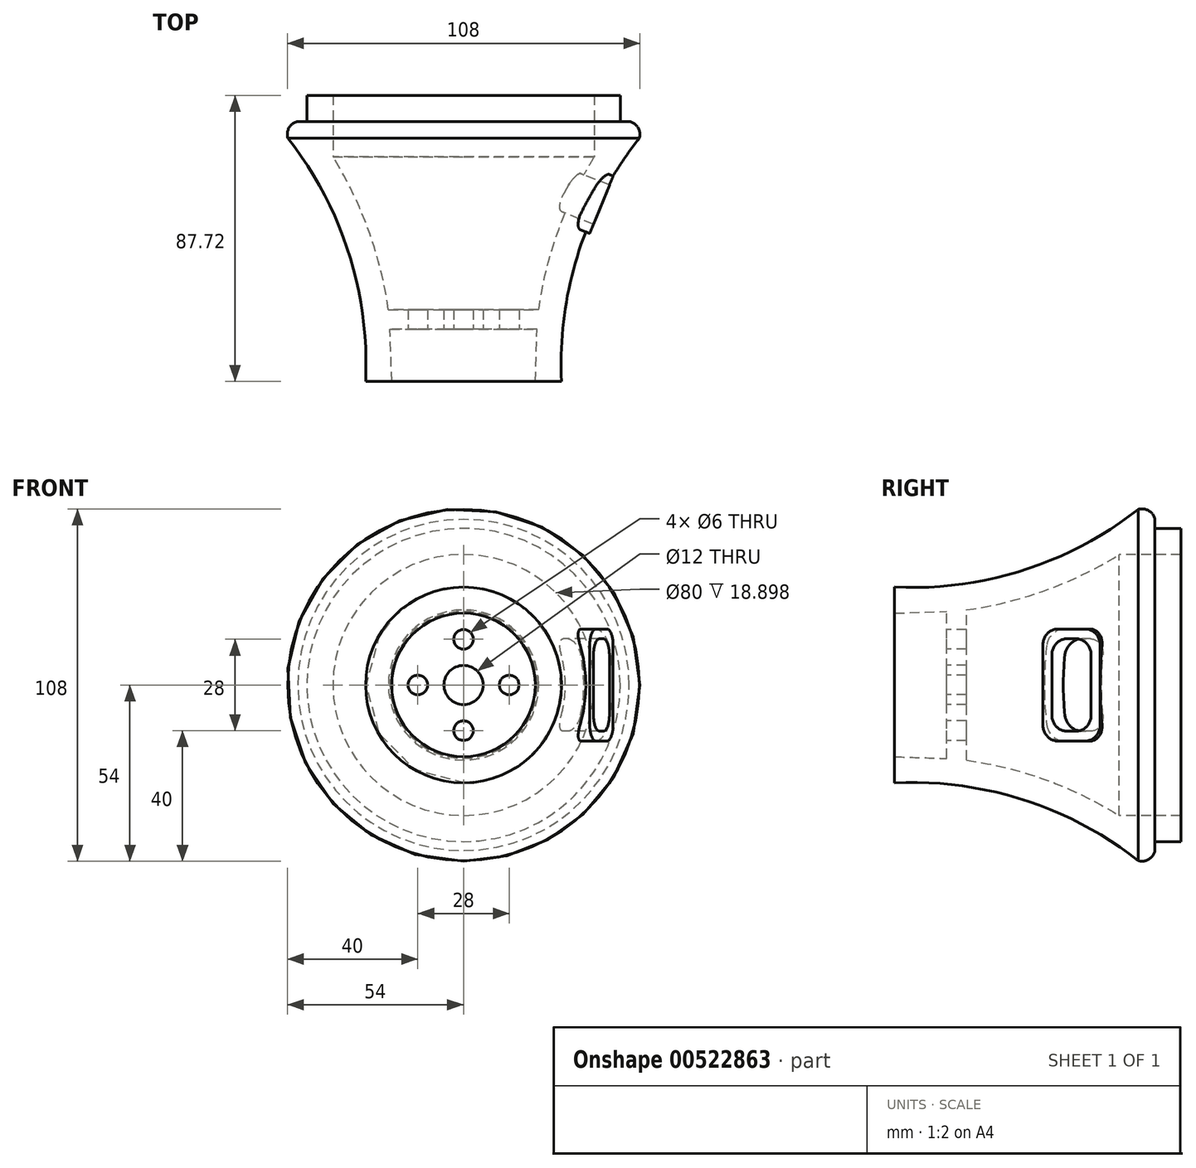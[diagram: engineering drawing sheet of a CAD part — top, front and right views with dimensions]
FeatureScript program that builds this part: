
annotation { "Feature Type Name" : "Feature", "Feature Type Description" : "" }
export const myFeature = defineFeature(function(context is Context, id is Id, definition is map)
    precondition{}
    {
        {
            var Q0;
            Q0=qCreatedBy(makeId("Top.planeOp"),FACE);
            var sketch = newSketch(context, id + "F0", { "sketchPlane" : qUnion([Q0])});
            skLineSegment(sketch, "E0", {"start": v(0, 0) * mm, "end": v(0, 16) * mm});
            skLineSegment(sketch, "E1", {"start": v(6, 16) * mm, "end": v(6, 22) * mm});
            skLineSegment(sketch, "E2", {"start": v(6, 22) * mm, "end": v(23.02, 22) * mm});
            skLineSegment(sketch, "E3", {"start": v(6, 16) * mm, "end": v(22.52, 16) * mm});
            skLineSegment(sketch, "E4", {"start": v(22, 0) * mm, "end": v(30, 0) * mm});
            skLineSegment(sketch, "E5.trimOffspring", {"start": v(0, 22) * mm, "end": v(0, 150) * mm});
            skLineSegment(sketch, "E6", {"start": v(22.52, 16) * mm, "end": v(22.25, 16) * mm});
            skLineSegment(sketch, "E7", {"start": v(40, 87.72) * mm, "end": v(48, 87.72) * mm});
            skArc(sketch, "E8", {"start": v(53.83, 74.63) * mm, "mid": v(53.43, 77.86) * mm, "end": v(50.76, 79.72) * mm});
            skLineSegment(sketch, "E9", {"start": v(48, 87.72) * mm, "end": v(48, 79.72) * mm});
            skLineSegment(sketch, "E10", {"start": v(50.76, 79.72) * mm, "end": v(48, 79.72) * mm});
            skArc(sketch, "E11", {"start": v(53.83, 74.63) * mm, "mid": v(35.17, 39.47) * mm, "end": v(30, 0) * mm});
            skArc(sketch, "E12.0", {"start": v(40, 68.83) * mm, "mid": v(29.06, 46.3) * mm, "end": v(23.02, 22) * mm});
            skLineSegment(sketch, "E13", {"start": v(22.52, 16) * mm, "end": v(22, 0) * mm});
            skPoint(sketch, "E14.end.orphan", {"position": v(52.08, 16) * mm});
            skLineSegment(sketch, "E15", {"start": v(40, 87.72) * mm, "end": v(40, 80) * mm});
            skLineSegment(sketch, "E16", {"start": v(40, 80) * mm, "end": v(40, 68.83) * mm});
            skPoint(sketch, "E17.orphan", {"position": v(0, 80) * mm});
            skLineSegment(sketch, "E18", {"start": v(0, 66) * mm, "end": v(38.3, 66) * mm});
            skPoint(sketch, "E19.trimOffspring.start.orphan", {"position": v(48, 75.8) * mm});
            skPoint(sketch, "E20.start.orphan", {"position": v(44.08, 22) * mm});
            skPoint(sketch, "E21.orphan", {"position": v(44.08, 16) * mm});
            skSolve(sketch);
        }
        {
            var Q0;
            Q0=makeQuery(id+"F0.imprint","IMPRINT",FACE,{"disambiguationData":[TD([[makeQuery(id+"F0.imprint","IMPRINT",EDGE,{"derivedFrom":sQuery(id+"F0.wireOp",EDGE,"E1")}),-1.0]])]});
            var Q1;
            Q1=sQuery(id+"F0.wireOp",EDGE,"E5.trimOffspring");
            revolve(context, id + "F1", {"entities" : qUnion([Q0]), "axis" : qUnion([Q1]), "revolveType" : RevolveType.FULL});
        }
        {
            var Q0;
            Q0=makeQuery(id+"F1.opRevolve","SWEPT_FACE",FACE,{"disambiguationData":[OSD([sQuery(id+"F0.wireOp",EDGE,"E3"),sQuery(id+"F0.wireOp",EDGE,"E6")])]});
            var sketch = newSketch(context, id + "F2", { "sketchPlane" : qUnion([Q0])});
            skArc(sketch, "E22", {"start": v(-13.68, -2.98) * mm, "mid": v(-9.9, -9.9) * mm, "end": v(-2.98, -13.68) * mm});
            skCircle(sketch, "E23", {"center": v(-14, 0) * mm, "radius": 3 * mm});
            skCircle(sketch, "E24.1.0", {"center": v(0, -14) * mm, "radius": 3 * mm});
            skCircle(sketch, "E24.2.0", {"center": v(14, 0) * mm, "radius": 3 * mm});
            skCircle(sketch, "E25.1.3.0", {"center": v(0, 14) * mm, "radius": 3 * mm});
            skArc(sketch, "E26.trimOffspring", {"start": v(-2.98, 13.68) * mm, "mid": v(-9.9, 9.9) * mm, "end": v(-13.68, 2.98) * mm});
            skArc(sketch, "E27.trimOffspring", {"start": v(13.68, 2.98) * mm, "mid": v(9.9, 9.9) * mm, "end": v(2.98, 13.68) * mm});
            skArc(sketch, "E28.trimOffspring", {"start": v(2.98, -13.68) * mm, "mid": v(9.9, -9.9) * mm, "end": v(13.68, -2.98) * mm});
            skSolve(sketch);
        }
        {
            var Q0;
            {var subQ0=sQuery(id+"F2.wireOp",EDGE,"E25.1.3.0");var subQ1=makeQuery(id+"F2.imprint","INTERSECT",VERTEX,{"derivedFrom":[subQ0,sQuery(id+"F2.wireOp",EDGE,"E26.trimOffspring")]});Q0=makeQuery(id+"F2.imprint","IMPRINT",FACE,{"disambiguationData":[TD([[makeQuery(id+"F2.imprint","IMPRINT",EDGE,{"disambiguationData":[TD([[subQ1,1.0]])],"derivedFrom":subQ0}),1.0]])]});}
            var Q1;
            {var subQ0=sQuery(id+"F2.wireOp",EDGE,"E24.2.0");var subQ1=makeQuery(id+"F2.imprint","INTERSECT",VERTEX,{"derivedFrom":[subQ0,sQuery(id+"F2.wireOp",EDGE,"E27.trimOffspring")]});Q1=makeQuery(id+"F2.imprint","IMPRINT",FACE,{"disambiguationData":[TD([[makeQuery(id+"F2.imprint","IMPRINT",EDGE,{"disambiguationData":[TD([[subQ1,1.0]])],"derivedFrom":subQ0}),1.0]])]});}
            var Q2;
            {var subQ0=sQuery(id+"F2.wireOp",EDGE,"E24.1.0");var subQ1=makeQuery(id+"F2.imprint","INTERSECT",VERTEX,{"derivedFrom":[sQuery(id+"F2.wireOp",EDGE,"E22"),subQ0]});Q2=makeQuery(id+"F2.imprint","IMPRINT",FACE,{"disambiguationData":[TD([[makeQuery(id+"F2.imprint","IMPRINT",EDGE,{"disambiguationData":[TD([[subQ1,-1.0]])],"derivedFrom":subQ0}),1.0]])]});}
            var Q3;
            {var subQ0=sQuery(id+"F2.wireOp",EDGE,"E23");var subQ1=makeQuery(id+"F2.imprint","INTERSECT",VERTEX,{"derivedFrom":[sQuery(id+"F2.wireOp",EDGE,"E22"),subQ0]});Q3=makeQuery(id+"F2.imprint","IMPRINT",FACE,{"disambiguationData":[TD([[makeQuery(id+"F2.imprint","IMPRINT",EDGE,{"disambiguationData":[TD([[subQ1,1.0]])],"derivedFrom":subQ0}),1.0]])]});}
            extrude(context, id + "F3", {"entities" : qUnion([Q0, Q1, Q2, Q3]), "operationType" : NewBodyOperationType.REMOVE, "oppositeDirection" : true, "depth" : 25 * mm, "offsetDistance" : 25 * mm});
        }
        {
            var Q0;
            Q0=qCreatedBy(makeId("Top.planeOp"),FACE);
            var sketch = newSketch(context, id + "F4", { "sketchPlane" : qUnion([Q0])});
            skLineSegment(sketch, "E29", {"start": v(-5.5, 66) * mm, "end": v(38.4, 66) * mm});
            skLineSegment(sketch, "E30", {"start": v(-5.5, 63) * mm, "end": v(-5.5, 66) * mm});
            skPoint(sketch, "E31.orphan", {"position": v(-6.76, 66) * mm});
            skLineSegment(sketch, "E32", {"start": v(0, 34) * mm, "end": v(25.39, 34) * mm});
            skLineSegment(sketch, "E33", {"start": v(25.39, 34) * mm, "end": v(38.4, 66) * mm});
            skSolve(sketch);
        }
        {
            var Q0;
            Q0=sQuery(id+"F4.wireOp",EDGE,"E33");
            cPlane(context, id + "F5", {"entities" : qUnion([Q0]), "cplaneType" : CPlaneType.LINE_ANGLE, "offset" : 25 * mm, "angle" : 90 * degree, "width" : 150 * mm, "height" : 150 * mm});
        }
        {
            var Q0;
            Q0=qCreatedBy(id+"F5.planeOp",FACE);
            var sketch = newSketch(context, id + "F6", { "sketchPlane" : qUnion([Q0])});
            skLineSegment(sketch, "E34", {"start": v(75.6, 0) * mm, "end": v(75.6, -12.17) * mm});
            skLineSegment(sketch, "E35", {"start": v(72.6, 0) * mm, "end": v(72.6, -9.17) * mm});
            skLineSegment(sketch, "E36", {"start": v(70.6, -17.17) * mm, "end": v(61.6, -17.17) * mm});
            skLineSegment(sketch, "E37", {"start": v(56.6, -12.17) * mm, "end": v(56.6, 0) * mm});
            skLineSegment(sketch, "E38", {"start": v(59.6, -9.17) * mm, "end": v(59.6, 0) * mm});
            skLineSegment(sketch, "E39", {"start": v(64.6, -14.17) * mm, "end": v(67.6, -14.17) * mm});
            skLineSegment(sketch, "E40.MirrorCS", {"start": v(75.6, 0) * mm, "end": v(75.6, 12.17) * mm});
            skLineSegment(sketch, "E41.MirrorCS", {"start": v(59.6, 9.17) * mm, "end": v(59.6, 0) * mm});
            skLineSegment(sketch, "E42.MirrorCS", {"start": v(72.6, 0) * mm, "end": v(72.6, 9.17) * mm});
            skLineSegment(sketch, "E43.MirrorCS", {"start": v(56.6, 12.17) * mm, "end": v(56.6, 0) * mm});
            skLineSegment(sketch, "E44.MirrorCS", {"start": v(64.6, 14.17) * mm, "end": v(67.6, 14.17) * mm});
            skLineSegment(sketch, "E45.MirrorCS", {"start": v(70.6, 17.17) * mm, "end": v(61.6, 17.17) * mm});
            skPoint(sketch, "E46.visualSharp", {"position": v(56.6, 17.17) * mm});
            skArc(sketch, "E46.filletArc", {"start": v(61.6, 17.17) * mm, "mid": v(58.07, 15.7) * mm, "end": v(56.6, 12.17) * mm});
            skPoint(sketch, "E47.visualSharp", {"position": v(75.6, 17.17) * mm});
            skArc(sketch, "E47.filletArc", {"start": v(75.6, 12.17) * mm, "mid": v(74.14, 15.7) * mm, "end": v(70.6, 17.17) * mm});
            skPoint(sketch, "E48.visualSharp", {"position": v(75.6, -17.17) * mm});
            skArc(sketch, "E48.filletArc", {"start": v(70.6, -17.17) * mm, "mid": v(74.14, -15.7) * mm, "end": v(75.6, -12.17) * mm});
            skPoint(sketch, "E49.visualSharp", {"position": v(56.6, -17.17) * mm});
            skArc(sketch, "E49.filletArc", {"start": v(56.6, -12.17) * mm, "mid": v(58.07, -15.7) * mm, "end": v(61.6, -17.17) * mm});
            skPoint(sketch, "E50.newPointA", {"position": v(59.6, -17) * mm});
            skPoint(sketch, "E50.newPointB", {"position": v(56.6, -14.17) * mm});
            skArc(sketch, "E50.filletArc", {"start": v(59.6, -9.17) * mm, "mid": v(61.07, -12.7) * mm, "end": v(64.6, -14.17) * mm});
            skPoint(sketch, "E51.newPointA", {"position": v(72.6, -17) * mm});
            skPoint(sketch, "E51.newPointB", {"position": v(75.6, -14.17) * mm});
            skArc(sketch, "E51.filletArc", {"start": v(67.6, -14.17) * mm, "mid": v(71.14, -12.7) * mm, "end": v(72.6, -9.17) * mm});
            skPoint(sketch, "E52.newPointA", {"position": v(72.6, 17) * mm});
            skPoint(sketch, "E52.newPointB", {"position": v(75.6, 14.17) * mm});
            skArc(sketch, "E52.filletArc", {"start": v(72.6, 9.17) * mm, "mid": v(71.14, 12.7) * mm, "end": v(67.6, 14.17) * mm});
            skPoint(sketch, "E53.newPointA", {"position": v(59.6, 17) * mm});
            skPoint(sketch, "E53.newPointB", {"position": v(56.6, 14.17) * mm});
            skArc(sketch, "E53.filletArc", {"start": v(64.6, 14.17) * mm, "mid": v(61.07, 12.7) * mm, "end": v(59.6, 9.17) * mm});
            skSolve(sketch);
        }
        {
            var Q0;
            Q0 = qSketchRegion(id + "F6", true);
            extrude(context, id + "F7", {"entities" : qUnion([Q0]), "operationType" : NewBodyOperationType.ADD, "depth" : 8 * mm, "offsetDistance" : 25 * mm});
        }
        {
            var Q0;
            Q0=makeQuery(id+"F6.imprint","IMPRINT",FACE,{"disambiguationData":[TD([[makeQuery(id+"F6.imprint","IMPRINT",EDGE,{"derivedFrom":sQuery(id+"F6.wireOp",EDGE,"E35")}),-1.0]])]});
            extrude(context, id + "F8", {"entities" : qUnion([Q0]), "operationType" : NewBodyOperationType.REMOVE, "endBound" : BoundingType.SYMMETRIC, "oppositeDirection" : true, "depth" : 25.4 * mm, "offsetDistance" : 25.4 * mm});
        }
    });
